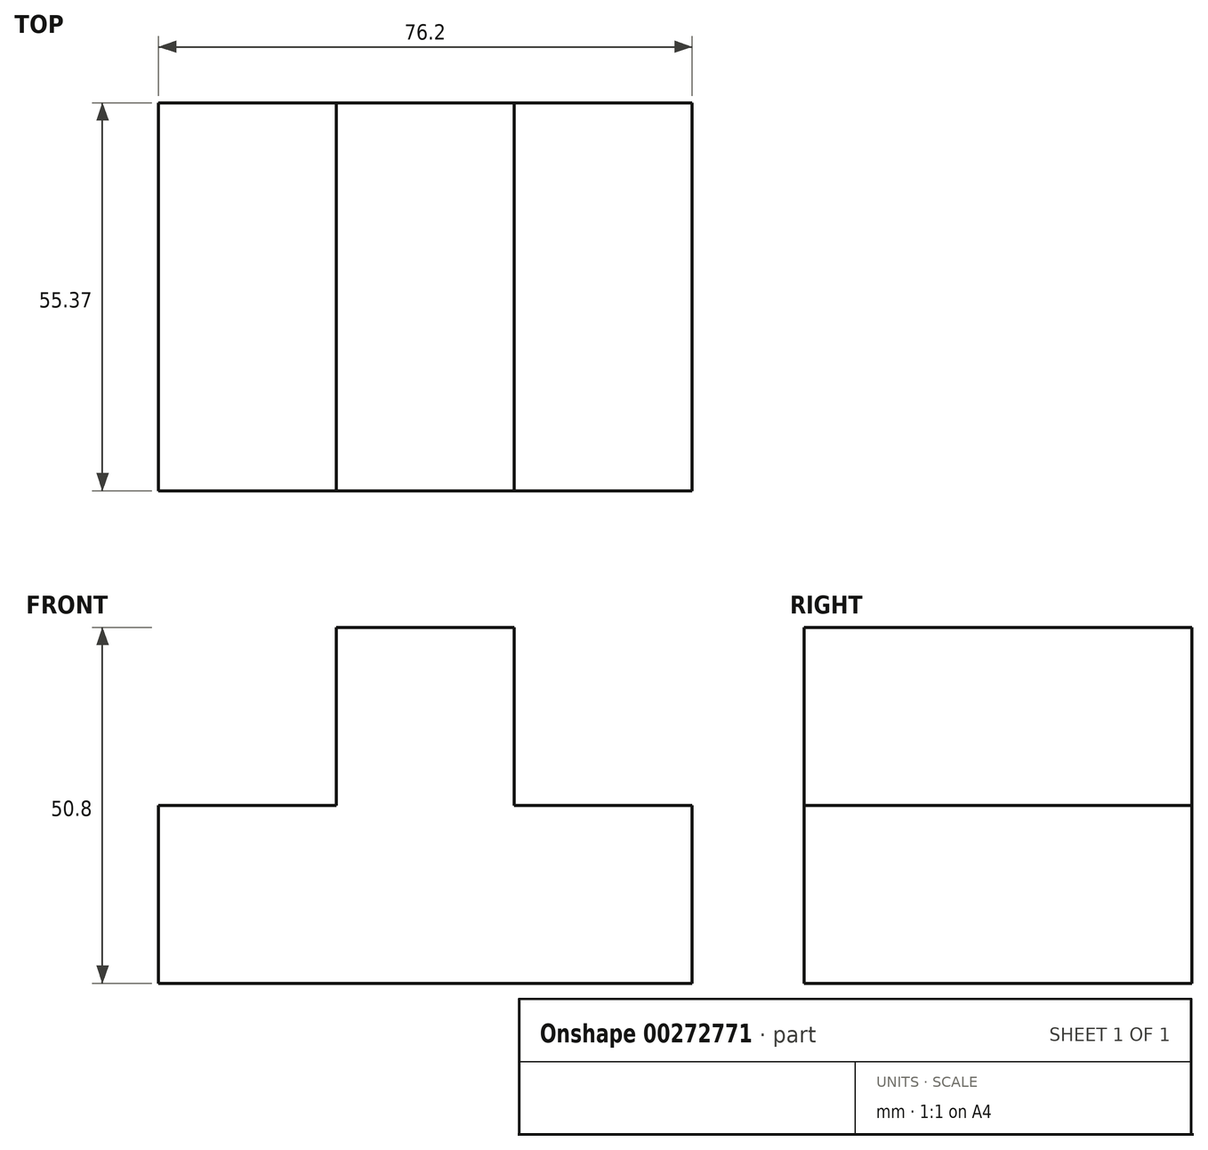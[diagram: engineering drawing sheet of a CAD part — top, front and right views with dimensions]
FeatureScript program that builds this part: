
annotation { "Feature Type Name" : "Feature", "Feature Type Description" : "" }
export const myFeature = defineFeature(function(context is Context, id is Id, definition is map)
    precondition{}
    {
        {
            var Q0;
            Q0=qCreatedBy(makeId("Front.planeOp"),FACE);
            var sketch = newSketch(context, id + "F0", { "sketchPlane" : qUnion([Q0])});
            skLineSegment(sketch, "E0", {"start": v(-28.95, -39.9) * mm, "end": v(47.25, -39.9) * mm});
            skLineSegment(sketch, "E1", {"start": v(47.25, -39.9) * mm, "end": v(47.25, -14.5) * mm});
            skLineSegment(sketch, "E2", {"start": v(47.25, -14.5) * mm, "end": v(21.85, -14.5) * mm});
            skLineSegment(sketch, "E3", {"start": v(21.85, -14.5) * mm, "end": v(21.85, 10.9) * mm});
            skLineSegment(sketch, "E4", {"start": v(21.85, 10.9) * mm, "end": v(-3.55, 10.9) * mm});
            skLineSegment(sketch, "E5", {"start": v(-3.55, 10.9) * mm, "end": v(-3.55, -14.5) * mm});
            skLineSegment(sketch, "E6", {"start": v(-3.55, -14.5) * mm, "end": v(-28.95, -14.5) * mm});
            skLineSegment(sketch, "E7", {"start": v(-28.95, -14.5) * mm, "end": v(-28.95, -39.9) * mm});
            skSolve(sketch);
        }
        {
            var Q0;
            Q0 = qSketchRegion(id + "F0", true);
            extrude(context, id + "F1", {"entities" : qUnion([Q0]), "depth" : 55.37 * mm});
        }
    });
